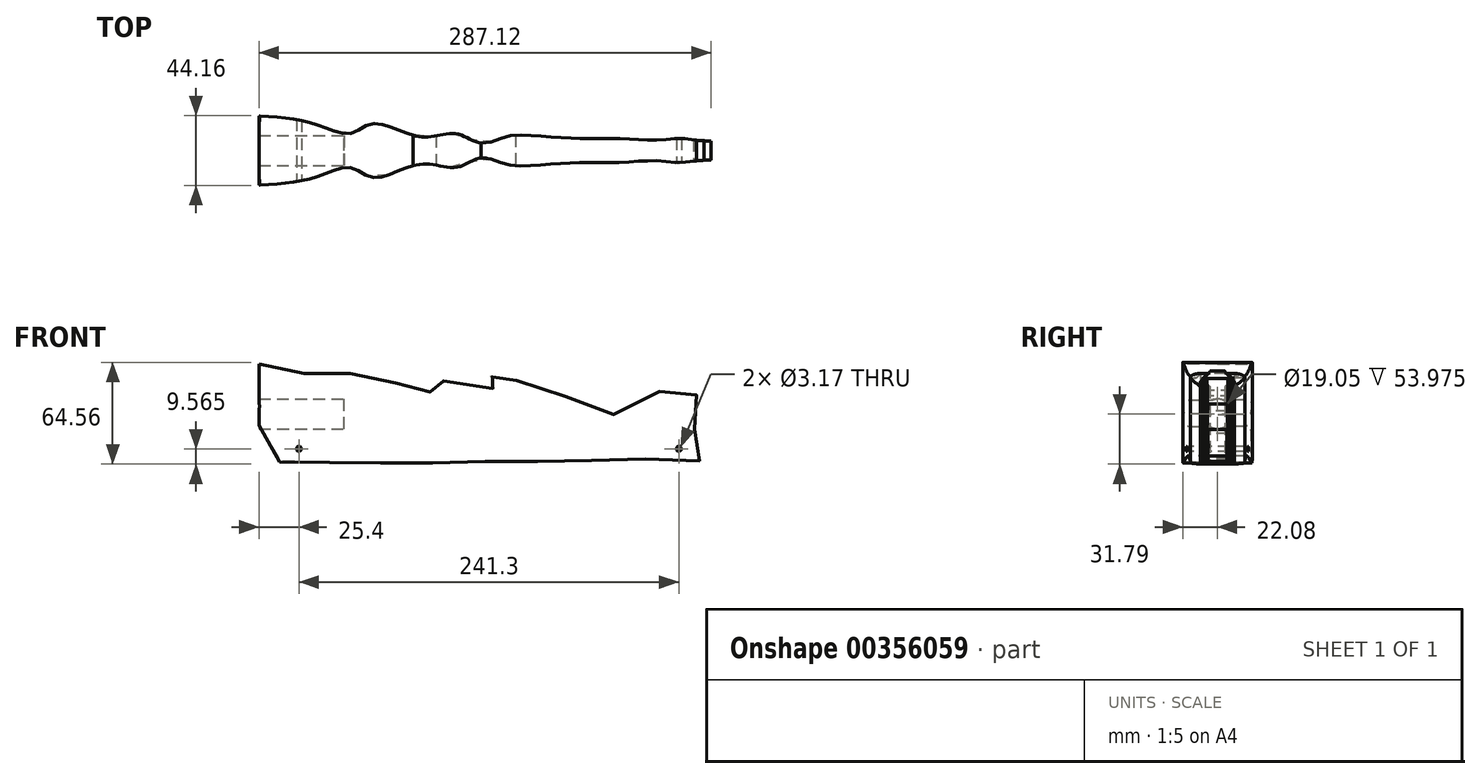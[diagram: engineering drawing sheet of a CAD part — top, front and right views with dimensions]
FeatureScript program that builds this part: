
annotation { "Feature Type Name" : "Feature", "Feature Type Description" : "" }
export const myFeature = defineFeature(function(context is Context, id is Id, definition is map)
    precondition{}
    {
        {
            var Q0;
            Q0=qCreatedBy(makeId("Front.planeOp"),FACE);
            var sketch = newSketch(context, id + "F0", { "sketchPlane" : qUnion([Q0])});
            skLineSegment(sketch, "E0.bottom", {"start": v(-146.25, 31.75) * mm, "end": v(145.85, 31.75) * mm, "construction": true});
            skLineSegment(sketch, "E0.top", {"start": v(-145.84, -31.75) * mm, "end": v(146.05, -31.75) * mm, "construction": true});
            skLineSegment(sketch, "E0.right", {"start": v(145.85, 31.75) * mm, "end": v(146.26, -31.75) * mm, "construction": true});
            skFitSpline(sketch, "E1", {"points": [v(-145.93, -17.7) * mm, v(-146.05, 0) * mm, v(-146.1, 9.19) * mm, v(-146.25, 31.75) * mm, v(-106.82, 22.95) * mm, v(-84.54, 25.73) * mm, v(-33.72, 11.59) * mm, v(-47.98, 21.77) * mm, v(16.97, 15.46) * mm, v(-4.62, 26.79) * mm, v(7.96, 23.98) * mm, v(55.73, 7.82) * mm, v(82.55, 0.48) * mm, v(130.07, 21.3) * mm, v(132.03, 2.03) * mm, v(136.62, 6.4) * mm, v(130.07, -12.07) * mm, v(136.62, -9.74) * mm, v(139.89, -25.64) * mm, v(119.36, -29.44) * mm, v(89.82, -28.75) * mm, v(73.54, -29.36) * mm, v(37.53, -30.03) * mm, v(21.43, -30.2) * mm, v(-7.91, -30.25) * mm, v(-27.1, -30.36) * mm, v(-44.01, -31.75) * mm, v(-92.95, -30.58) * mm, v(-111.54, -29.6) * mm, v(-116.2, -26.77) * mm, v(-142.25, -30.85) * mm, v(-145.93, -17.7) * mm]});
            skLineSegment(sketch, "E2.bottom", {"start": v(-146.1, 9.52) * mm, "end": v(-95.3, 9.52) * mm, "construction": true});
            skLineSegment(sketch, "E2.top", {"start": v(-145.99, -9.52) * mm, "end": v(-95.18, -9.52) * mm, "construction": true});
            skLineSegment(sketch, "E2.right", {"start": v(-95.3, 9.52) * mm, "end": v(-95.18, -9.52) * mm, "construction": true});
            skLineSegment(sketch, "E3", {"start": v(-146.25, 31.75) * mm, "end": v(-145.84, -31.75) * mm, "construction": true});
            skPoint(sketch, "E4", {"position": v(-0.2, 31.75) * mm});
            skPoint(sketch, "E5", {"position": v(146.14, 0.02) * mm});
            skSolve(sketch);
        }
        {
            var Q0;
            Q0=qCreatedBy(makeId("Top.planeOp"),FACE);
            var sketch = newSketch(context, id + "F1", { "sketchPlane" : qUnion([Q0])});
            skLineSegment(sketch, "E6.bottom", {"start": v(-146.05, 22.22) * mm, "end": v(146.05, 22.23) * mm, "construction": true});
            skLineSegment(sketch, "E6.top", {"start": v(-146.05, -22.23) * mm, "end": v(146.05, -22.22) * mm, "construction": true});
            skLineSegment(sketch, "E6.left", {"start": v(-146.05, 22.22) * mm, "end": v(-146.05, -22.23) * mm, "construction": true});
            skLineSegment(sketch, "E6.right", {"start": v(146.05, 22.22) * mm, "end": v(146.05, -22.22) * mm, "construction": true});
            skLineSegment(sketch, "E7", {"start": v(-146.05, 0) * mm, "end": v(146.05, 0) * mm, "construction": true});
            skFitSpline(sketch, "E8", {"points": [v(-146.05, 0) * mm, v(-146.05, 19.96) * mm, v(-145.72, 21.88) * mm, v(-142.08, 21.86) * mm, v(-113.31, 17.8) * mm, v(-87.68, 10.88) * mm, v(-73.36, 17.24) * mm, v(-43.88, 8.81) * mm, v(-21.38, 10.75) * mm, v(-8.98, 5.77) * mm, v(0, 5.14) * mm, v(12.52, 9.17) * mm, v(31.78, 9.2) * mm, v(59.2, 7.55) * mm, v(80.04, 7.67) * mm, v(108.27, 6.57) * mm, v(120.14, 7.82) * mm, v(133.74, 6.3) * mm, v(142.8, 5.45) * mm, v(146.05, 0) * mm], "startDerivative": vector(0, 335.54) * mm, "endDerivative": vector(0, -277.49) * mm});
            skFitSpline(sketch, "E9.MirrorCS", {"points": [v(-146.05, 0) * mm, v(-146.05, -19.96) * mm, v(-145.72, -21.88) * mm, v(-142.08, -21.86) * mm, v(-113.31, -17.8) * mm, v(-87.68, -10.88) * mm, v(-73.36, -17.24) * mm, v(-43.88, -8.81) * mm, v(-21.38, -10.75) * mm, v(-8.98, -5.77) * mm, v(0, -5.14) * mm, v(12.52, -9.17) * mm, v(31.78, -9.2) * mm, v(59.2, -7.55) * mm, v(80.04, -7.67) * mm, v(108.27, -6.57) * mm, v(120.14, -7.82) * mm, v(133.74, -6.3) * mm, v(142.8, -5.45) * mm, v(146.05, 0) * mm], "startDerivative": vector(0, -335.54) * mm, "endDerivative": vector(0, 277.49) * mm});
            skLineSegment(sketch, "E10.MirrorCS", {"start": v(-146.05, -22.23) * mm, "end": v(146.05, -22.23) * mm});
            skSolve(sketch);
        }
        {
            var Q0;
            Q0=qCreatedBy(makeId("Right.planeOp"),FACE);
            var sketch = newSketch(context, id + "F2", { "sketchPlane" : qUnion([Q0])});
            skCircle(sketch, "E11", {"center": v(0, 0) * mm, "radius": 9.53 * mm});
            skSolve(sketch);
        }
        {
            var Q0;
            Q0=qCreatedBy(makeId("Front.planeOp"),FACE);
            var sketch = newSketch(context, id + "F3", { "sketchPlane" : qUnion([Q0])});
            skCircle(sketch, "E12", {"center": v(-120.65, -22.22) * mm, "radius": 1.59 * mm});
            skCircle(sketch, "E13", {"center": v(120.65, -22.23) * mm, "radius": 1.59 * mm});
            skSolve(sketch);
        }
        {
            var Q0;
            Q0=qSketchRegion(id+"F0",true);
            extrude(context, id + "F4", {"entities" : qUnion([Q0]), "depth" : 44.45 * mm, "symmetric" : true});
        }
        {
            var Q0;
            Q0=qSketchRegion(id+"F1",true);
            extrude(context, id + "F5", {"entities" : qUnion([Q0]), "operationType" : NewBodyOperationType.INTERSECT, "endBound" : BoundingType.THROUGH_ALL, "oppositeDirection" : true, "depth" : 60.96 * mm, "hasSecondDirection" : true, "secondDirectionBound" : BoundingType.THROUGH_ALL, "secondDirectionOppositeDirection" : false, "secondDirectionDepth" : 25.4 * mm});
        }
        {
            var Q0;
            Q0=qSketchRegion(id+"F2",true);
            extrude(context, id + "F6", {"entities" : qUnion([Q0]), "operationType" : NewBodyOperationType.REMOVE, "oppositeDirection" : true, "depth" : 152.4 * mm, "hasSecondDirection" : true, "secondDirectionOppositeDirection" : true, "secondDirectionDepth" : 92.07 * mm});
        }
        {
            var Q0;
            Q0=qSketchRegion(id+"F3",true);
            extrude(context, id + "F7", {"entities" : qUnion([Q0]), "operationType" : NewBodyOperationType.REMOVE, "oppositeDirection" : true, "depth" : 50.8 * mm, "symmetric" : true});
        }
    });
